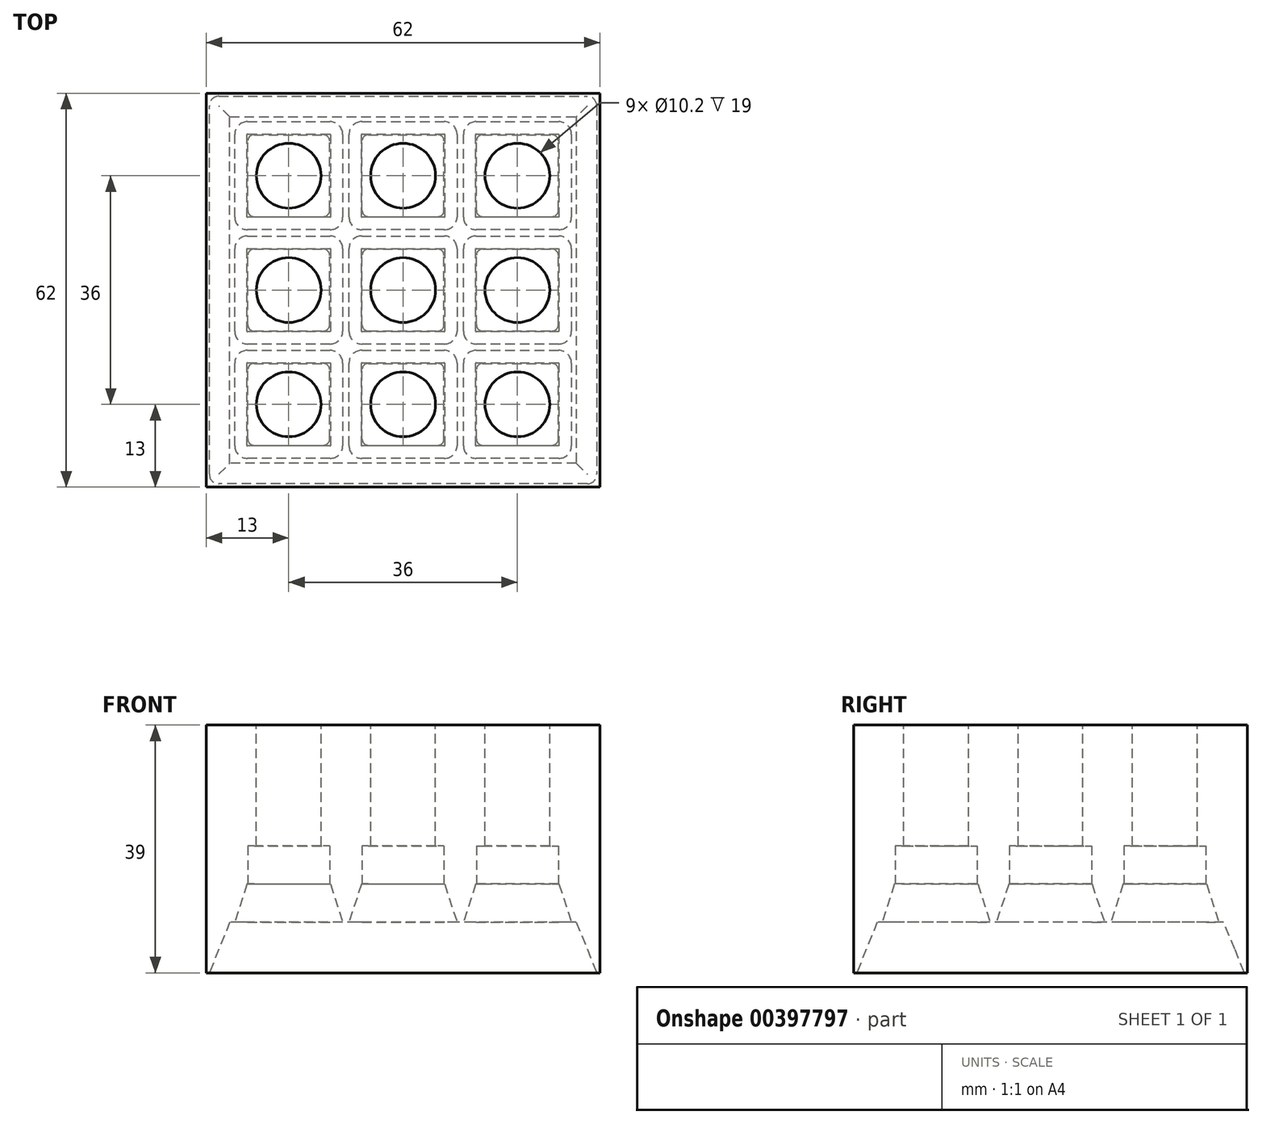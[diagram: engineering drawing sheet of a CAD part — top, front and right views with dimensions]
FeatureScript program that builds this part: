
annotation { "Feature Type Name" : "Feature", "Feature Type Description" : "" }
export const myFeature = defineFeature(function(context is Context, id is Id, definition is map)
    precondition{}
    {
        {
            var Q0;
            Q0=qCreatedBy(makeId("Top.planeOp"),FACE);
            var sketch = newSketch(context, id + "F0", { "sketchPlane" : qUnion([Q0])});
            skLineSegment(sketch, "E0.bottom", {"start": v(-31, 31) * mm, "end": v(31, 31) * mm});
            skLineSegment(sketch, "E0.top", {"start": v(-31, -31) * mm, "end": v(31, -31) * mm});
            skLineSegment(sketch, "E0.left", {"start": v(-31, 31) * mm, "end": v(-31, -31) * mm});
            skLineSegment(sketch, "E0.right", {"start": v(31, 31) * mm, "end": v(31, -31) * mm});
            skPoint(sketch, "E0.middle", {"position": v(0, 0) * mm});
            skSolve(sketch);
        }
        {
            var Q0;
            Q0=makeQuery(id+"F0.imprint","IMPRINT",FACE,{"disambiguationData":[TD([[makeQuery(id+"F0.imprint","IMPRINT",EDGE,{"derivedFrom":sQuery(id+"F0.wireOp",EDGE,"E0.bottom")}),-1.0]])]});
            extrude(context, id + "F1", {"entities" : qUnion([Q0]), "depth" : 39 * mm});
        }
        {
            var Q0;
            Q0=qCreatedBy(makeId("Top.planeOp"),FACE);
            cPlane(context, id + "F2", {"entities" : qUnion([Q0]), "cplaneType" : CPlaneType.OFFSET, "offset" : 8 * mm, "width" : 150 * mm, "height" : 150 * mm});
        }
        {
            var Q0;
            Q0=qCreatedBy(makeId("Top.planeOp"),FACE);
            var sketch = newSketch(context, id + "F3", { "sketchPlane" : qUnion([Q0])});
            skLineSegment(sketch, "E1.bottom", {"start": v(29, 30.5) * mm, "end": v(-29, 30.5) * mm});
            skLineSegment(sketch, "E1.top", {"start": v(29, -30.5) * mm, "end": v(-29, -30.5) * mm});
            skLineSegment(sketch, "E1.left", {"start": v(30.5, 29) * mm, "end": v(30.5, -29) * mm});
            skLineSegment(sketch, "E1.right", {"start": v(-30.5, 29) * mm, "end": v(-30.5, -29) * mm});
            skPoint(sketch, "E1.middle", {"position": v(0, 0) * mm});
            skPoint(sketch, "E2.visualSharp", {"position": v(30.5, -30.5) * mm});
            skArc(sketch, "E2.filletArc", {"start": v(29, -30.5) * mm, "mid": v(30.06, -30.06) * mm, "end": v(30.5, -29) * mm});
            skPoint(sketch, "E3.visualSharp", {"position": v(30.5, 30.5) * mm});
            skArc(sketch, "E3.filletArc", {"start": v(30.5, 29) * mm, "mid": v(30.06, 30.06) * mm, "end": v(29, 30.5) * mm});
            skPoint(sketch, "E4.visualSharp", {"position": v(-30.5, 30.5) * mm});
            skArc(sketch, "E4.filletArc", {"start": v(-29, 30.5) * mm, "mid": v(-30.06, 30.06) * mm, "end": v(-30.5, 29) * mm});
            skPoint(sketch, "E5.visualSharp", {"position": v(-30.5, -30.5) * mm});
            skArc(sketch, "E5.filletArc", {"start": v(-30.5, -29) * mm, "mid": v(-30.06, -30.06) * mm, "end": v(-29, -30.5) * mm});
            skSolve(sketch);
        }
        {
            var Q0;
            Q0 = qSketchRegion(id + "F3", true);
            extrude(context, id + "F4", {"entities" : qUnion([Q0]), "operationType" : NewBodyOperationType.REMOVE, "depth" : 8 * mm, "hasDraft" : true, "draftAngle" : 22 * degree, "draftPullDirection" : true});
        }
        {
            var Q0;
            Q0=qCreatedBy(id+"F2.planeOp",FACE);
            var sketch = newSketch(context, id + "F5", { "sketchPlane" : qUnion([Q0])});
            skLineSegment(sketch, "E6", {"start": v(0, -40.1) * mm, "end": v(0, 43.6) * mm, "construction": true});
            skLineSegment(sketch, "E7", {"start": v(42.56, 0) * mm, "end": v(-45.4, 0) * mm, "construction": true});
            skLineSegment(sketch, "E8", {"start": v(-18, -41.12) * mm, "end": v(-18, 43.04) * mm, "construction": true});
            skLineSegment(sketch, "E9", {"start": v(18, -41.98) * mm, "end": v(18, 43.76) * mm, "construction": true});
            skLineSegment(sketch, "E10", {"start": v(-42.81, -18) * mm, "end": v(38.4, -18) * mm, "construction": true});
            skLineSegment(sketch, "E11", {"start": v(-40.82, 18) * mm, "end": v(38.75, 18) * mm, "construction": true});
            skLineSegment(sketch, "E12.bottom", {"start": v(11.5, -9.5) * mm, "end": v(24.5, -9.5) * mm});
            skLineSegment(sketch, "E12.top", {"start": v(11.5, -26.5) * mm, "end": v(24.5, -26.5) * mm});
            skLineSegment(sketch, "E12.left", {"start": v(9.5, -11.5) * mm, "end": v(9.5, -24.5) * mm});
            skLineSegment(sketch, "E12.right", {"start": v(26.5, -11.5) * mm, "end": v(26.5, -24.5) * mm});
            skPoint(sketch, "E12.middle", {"position": v(18, -18) * mm});
            skPoint(sketch, "E13.visualSharp", {"position": v(26.5, -26.5) * mm});
            skArc(sketch, "E13.filletArc", {"start": v(24.5, -26.5) * mm, "mid": v(25.91, -25.91) * mm, "end": v(26.5, -24.5) * mm});
            skPoint(sketch, "E14.visualSharp", {"position": v(26.5, -9.5) * mm});
            skArc(sketch, "E14.filletArc", {"start": v(26.5, -11.5) * mm, "mid": v(25.91, -10.09) * mm, "end": v(24.5, -9.5) * mm});
            skPoint(sketch, "E15.visualSharp", {"position": v(9.5, -9.5) * mm});
            skArc(sketch, "E15.filletArc", {"start": v(11.5, -9.5) * mm, "mid": v(10.09, -10.09) * mm, "end": v(9.5, -11.5) * mm});
            skPoint(sketch, "E16.visualSharp", {"position": v(9.5, -26.5) * mm});
            skArc(sketch, "E16.filletArc", {"start": v(9.5, -24.5) * mm, "mid": v(10.09, -25.91) * mm, "end": v(11.5, -26.5) * mm});
            skPoint(sketch, "E17.0.1.0", {"position": v(9.5, 8.5) * mm});
            skPoint(sketch, "E17.0.1.1", {"position": v(9.5, -8.5) * mm});
            skPoint(sketch, "E17.0.1.2", {"position": v(26.5, -8.5) * mm});
            skPoint(sketch, "E17.0.1.3", {"position": v(26.5, 8.5) * mm});
            skPoint(sketch, "E17.0.1.4", {"position": v(18, 0) * mm});
            skLineSegment(sketch, "E17.0.1.5", {"start": v(26.5, 6.5) * mm, "end": v(26.5, -6.5) * mm});
            skLineSegment(sketch, "E17.0.1.6", {"start": v(9.5, 6.5) * mm, "end": v(9.5, -6.5) * mm});
            skLineSegment(sketch, "E17.0.1.7", {"start": v(11.5, 8.5) * mm, "end": v(24.5, 8.5) * mm});
            skLineSegment(sketch, "E17.0.1.8", {"start": v(11.5, -8.5) * mm, "end": v(24.5, -8.5) * mm});
            skArc(sketch, "E17.0.1.9", {"start": v(26.5, 6.5) * mm, "mid": v(25.91, 7.91) * mm, "end": v(24.5, 8.5) * mm});
            skArc(sketch, "E17.0.1.10", {"start": v(24.5, -8.5) * mm, "mid": v(25.91, -7.91) * mm, "end": v(26.5, -6.5) * mm});
            skArc(sketch, "E17.0.1.11", {"start": v(11.5, 8.5) * mm, "mid": v(10.09, 7.91) * mm, "end": v(9.5, 6.5) * mm});
            skArc(sketch, "E17.0.1.12", {"start": v(9.5, -6.5) * mm, "mid": v(10.09, -7.91) * mm, "end": v(11.5, -8.5) * mm});
            skPoint(sketch, "E17.0.2.0", {"position": v(9.5, 26.5) * mm});
            skPoint(sketch, "E17.0.2.1", {"position": v(9.5, 9.5) * mm});
            skPoint(sketch, "E17.0.2.2", {"position": v(26.5, 9.5) * mm});
            skPoint(sketch, "E17.0.2.3", {"position": v(26.5, 26.5) * mm});
            skPoint(sketch, "E17.0.2.4", {"position": v(18, 18) * mm});
            skLineSegment(sketch, "E17.0.2.5", {"start": v(26.5, 24.5) * mm, "end": v(26.5, 11.5) * mm});
            skLineSegment(sketch, "E17.0.2.6", {"start": v(9.5, 24.5) * mm, "end": v(9.5, 11.5) * mm});
            skLineSegment(sketch, "E17.0.2.7", {"start": v(11.5, 26.5) * mm, "end": v(24.5, 26.5) * mm});
            skLineSegment(sketch, "E17.0.2.8", {"start": v(11.5, 9.5) * mm, "end": v(24.5, 9.5) * mm});
            skArc(sketch, "E17.0.2.9", {"start": v(26.5, 24.5) * mm, "mid": v(25.91, 25.91) * mm, "end": v(24.5, 26.5) * mm});
            skArc(sketch, "E17.0.2.10", {"start": v(24.5, 9.5) * mm, "mid": v(25.91, 10.09) * mm, "end": v(26.5, 11.5) * mm});
            skArc(sketch, "E17.0.2.11", {"start": v(11.5, 26.5) * mm, "mid": v(10.09, 25.91) * mm, "end": v(9.5, 24.5) * mm});
            skArc(sketch, "E17.0.2.12", {"start": v(9.5, 11.5) * mm, "mid": v(10.09, 10.09) * mm, "end": v(11.5, 9.5) * mm});
            skPoint(sketch, "E17.1.0.0", {"position": v(-8.5, -9.5) * mm});
            skPoint(sketch, "E17.1.0.1", {"position": v(-8.5, -26.5) * mm});
            skPoint(sketch, "E17.1.0.2", {"position": v(8.5, -26.5) * mm});
            skPoint(sketch, "E17.1.0.3", {"position": v(8.5, -9.5) * mm});
            skPoint(sketch, "E17.1.0.4", {"position": v(0, -18) * mm});
            skLineSegment(sketch, "E17.1.0.5", {"start": v(8.5, -11.5) * mm, "end": v(8.5, -24.5) * mm});
            skLineSegment(sketch, "E17.1.0.6", {"start": v(-8.5, -11.5) * mm, "end": v(-8.5, -24.5) * mm});
            skLineSegment(sketch, "E17.1.0.7", {"start": v(-6.5, -9.5) * mm, "end": v(6.5, -9.5) * mm});
            skLineSegment(sketch, "E17.1.0.8", {"start": v(-6.5, -26.5) * mm, "end": v(6.5, -26.5) * mm});
            skArc(sketch, "E17.1.0.9", {"start": v(8.5, -11.5) * mm, "mid": v(7.91, -10.09) * mm, "end": v(6.5, -9.5) * mm});
            skArc(sketch, "E17.1.0.10", {"start": v(6.5, -26.5) * mm, "mid": v(7.91, -25.91) * mm, "end": v(8.5, -24.5) * mm});
            skArc(sketch, "E17.1.0.11", {"start": v(-6.5, -9.5) * mm, "mid": v(-7.91, -10.09) * mm, "end": v(-8.5, -11.5) * mm});
            skArc(sketch, "E17.1.0.12", {"start": v(-8.5, -24.5) * mm, "mid": v(-7.91, -25.91) * mm, "end": v(-6.5, -26.5) * mm});
            skPoint(sketch, "E17.1.1.0", {"position": v(-8.5, 8.5) * mm});
            skPoint(sketch, "E17.1.1.1", {"position": v(-8.5, -8.5) * mm});
            skPoint(sketch, "E17.1.1.2", {"position": v(8.5, -8.5) * mm});
            skPoint(sketch, "E17.1.1.3", {"position": v(8.5, 8.5) * mm});
            skPoint(sketch, "E17.1.1.4", {"position": v(0, 0) * mm});
            skLineSegment(sketch, "E17.1.1.5", {"start": v(8.5, 6.5) * mm, "end": v(8.5, -6.5) * mm});
            skLineSegment(sketch, "E17.1.1.6", {"start": v(-8.5, 6.5) * mm, "end": v(-8.5, -6.5) * mm});
            skLineSegment(sketch, "E17.1.1.7", {"start": v(-6.5, 8.5) * mm, "end": v(6.5, 8.5) * mm});
            skLineSegment(sketch, "E17.1.1.8", {"start": v(-6.5, -8.5) * mm, "end": v(6.5, -8.5) * mm});
            skArc(sketch, "E17.1.1.9", {"start": v(8.5, 6.5) * mm, "mid": v(7.91, 7.91) * mm, "end": v(6.5, 8.5) * mm});
            skArc(sketch, "E17.1.1.10", {"start": v(6.5, -8.5) * mm, "mid": v(7.91, -7.91) * mm, "end": v(8.5, -6.5) * mm});
            skArc(sketch, "E17.1.1.11", {"start": v(-6.5, 8.5) * mm, "mid": v(-7.91, 7.91) * mm, "end": v(-8.5, 6.5) * mm});
            skArc(sketch, "E17.1.1.12", {"start": v(-8.5, -6.5) * mm, "mid": v(-7.91, -7.91) * mm, "end": v(-6.5, -8.5) * mm});
            skPoint(sketch, "E17.1.2.0", {"position": v(-8.5, 26.5) * mm});
            skPoint(sketch, "E17.1.2.1", {"position": v(-8.5, 9.5) * mm});
            skPoint(sketch, "E17.1.2.2", {"position": v(8.5, 9.5) * mm});
            skPoint(sketch, "E17.1.2.3", {"position": v(8.5, 26.5) * mm});
            skPoint(sketch, "E17.1.2.4", {"position": v(0, 18) * mm});
            skLineSegment(sketch, "E17.1.2.5", {"start": v(8.5, 24.5) * mm, "end": v(8.5, 11.5) * mm});
            skLineSegment(sketch, "E17.1.2.6", {"start": v(-8.5, 24.5) * mm, "end": v(-8.5, 11.5) * mm});
            skLineSegment(sketch, "E17.1.2.7", {"start": v(-6.5, 26.5) * mm, "end": v(6.5, 26.5) * mm});
            skLineSegment(sketch, "E17.1.2.8", {"start": v(-6.5, 9.5) * mm, "end": v(6.5, 9.5) * mm});
            skArc(sketch, "E17.1.2.9", {"start": v(8.5, 24.5) * mm, "mid": v(7.91, 25.91) * mm, "end": v(6.5, 26.5) * mm});
            skArc(sketch, "E17.1.2.10", {"start": v(6.5, 9.5) * mm, "mid": v(7.91, 10.09) * mm, "end": v(8.5, 11.5) * mm});
            skArc(sketch, "E17.1.2.11", {"start": v(-6.5, 26.5) * mm, "mid": v(-7.91, 25.91) * mm, "end": v(-8.5, 24.5) * mm});
            skArc(sketch, "E17.1.2.12", {"start": v(-8.5, 11.5) * mm, "mid": v(-7.91, 10.09) * mm, "end": v(-6.5, 9.5) * mm});
            skPoint(sketch, "E17.2.0.0", {"position": v(-26.5, -9.5) * mm});
            skPoint(sketch, "E17.2.0.1", {"position": v(-26.5, -26.5) * mm});
            skPoint(sketch, "E17.2.0.2", {"position": v(-9.5, -26.5) * mm});
            skPoint(sketch, "E17.2.0.3", {"position": v(-9.5, -9.5) * mm});
            skPoint(sketch, "E17.2.0.4", {"position": v(-18, -18) * mm});
            skLineSegment(sketch, "E17.2.0.5", {"start": v(-9.5, -11.5) * mm, "end": v(-9.5, -24.5) * mm});
            skLineSegment(sketch, "E17.2.0.6", {"start": v(-26.5, -11.5) * mm, "end": v(-26.5, -24.5) * mm});
            skLineSegment(sketch, "E17.2.0.7", {"start": v(-24.5, -9.5) * mm, "end": v(-11.5, -9.5) * mm});
            skLineSegment(sketch, "E17.2.0.8", {"start": v(-24.5, -26.5) * mm, "end": v(-11.5, -26.5) * mm});
            skArc(sketch, "E17.2.0.9", {"start": v(-9.5, -11.5) * mm, "mid": v(-10.09, -10.09) * mm, "end": v(-11.5, -9.5) * mm});
            skArc(sketch, "E17.2.0.10", {"start": v(-11.5, -26.5) * mm, "mid": v(-10.09, -25.91) * mm, "end": v(-9.5, -24.5) * mm});
            skArc(sketch, "E17.2.0.11", {"start": v(-24.5, -9.5) * mm, "mid": v(-25.91, -10.09) * mm, "end": v(-26.5, -11.5) * mm});
            skArc(sketch, "E17.2.0.12", {"start": v(-26.5, -24.5) * mm, "mid": v(-25.91, -25.91) * mm, "end": v(-24.5, -26.5) * mm});
            skPoint(sketch, "E17.2.1.0", {"position": v(-26.5, 8.5) * mm});
            skPoint(sketch, "E17.2.1.1", {"position": v(-26.5, -8.5) * mm});
            skPoint(sketch, "E17.2.1.2", {"position": v(-9.5, -8.5) * mm});
            skPoint(sketch, "E17.2.1.3", {"position": v(-9.5, 8.5) * mm});
            skPoint(sketch, "E17.2.1.4", {"position": v(-18, 0) * mm});
            skLineSegment(sketch, "E17.2.1.5", {"start": v(-9.5, 6.5) * mm, "end": v(-9.5, -6.5) * mm});
            skLineSegment(sketch, "E17.2.1.6", {"start": v(-26.5, 6.5) * mm, "end": v(-26.5, -6.5) * mm});
            skLineSegment(sketch, "E17.2.1.7", {"start": v(-24.5, 8.5) * mm, "end": v(-11.5, 8.5) * mm});
            skLineSegment(sketch, "E17.2.1.8", {"start": v(-24.5, -8.5) * mm, "end": v(-11.5, -8.5) * mm});
            skArc(sketch, "E17.2.1.9", {"start": v(-9.5, 6.5) * mm, "mid": v(-10.09, 7.91) * mm, "end": v(-11.5, 8.5) * mm});
            skArc(sketch, "E17.2.1.10", {"start": v(-11.5, -8.5) * mm, "mid": v(-10.09, -7.91) * mm, "end": v(-9.5, -6.5) * mm});
            skArc(sketch, "E17.2.1.11", {"start": v(-24.5, 8.5) * mm, "mid": v(-25.91, 7.91) * mm, "end": v(-26.5, 6.5) * mm});
            skArc(sketch, "E17.2.1.12", {"start": v(-26.5, -6.5) * mm, "mid": v(-25.91, -7.91) * mm, "end": v(-24.5, -8.5) * mm});
            skPoint(sketch, "E17.2.2.0", {"position": v(-26.5, 26.5) * mm});
            skPoint(sketch, "E17.2.2.1", {"position": v(-26.5, 9.5) * mm});
            skPoint(sketch, "E17.2.2.2", {"position": v(-9.5, 9.5) * mm});
            skPoint(sketch, "E17.2.2.3", {"position": v(-9.5, 26.5) * mm});
            skPoint(sketch, "E17.2.2.4", {"position": v(-18, 18) * mm});
            skLineSegment(sketch, "E17.2.2.5", {"start": v(-9.5, 24.5) * mm, "end": v(-9.5, 11.5) * mm});
            skLineSegment(sketch, "E17.2.2.6", {"start": v(-26.5, 24.5) * mm, "end": v(-26.5, 11.5) * mm});
            skLineSegment(sketch, "E17.2.2.7", {"start": v(-24.5, 26.5) * mm, "end": v(-11.5, 26.5) * mm});
            skLineSegment(sketch, "E17.2.2.8", {"start": v(-24.5, 9.5) * mm, "end": v(-11.5, 9.5) * mm});
            skArc(sketch, "E17.2.2.9", {"start": v(-9.5, 24.5) * mm, "mid": v(-10.09, 25.91) * mm, "end": v(-11.5, 26.5) * mm});
            skArc(sketch, "E17.2.2.10", {"start": v(-11.5, 9.5) * mm, "mid": v(-10.09, 10.09) * mm, "end": v(-9.5, 11.5) * mm});
            skArc(sketch, "E17.2.2.11", {"start": v(-24.5, 26.5) * mm, "mid": v(-25.91, 25.91) * mm, "end": v(-26.5, 24.5) * mm});
            skArc(sketch, "E17.2.2.12", {"start": v(-26.5, 11.5) * mm, "mid": v(-25.91, 10.09) * mm, "end": v(-24.5, 9.5) * mm});
            skLineSegment(sketch, "E17.direction1", {"start": v(9.5, -26.5) * mm, "end": v(-8.5, -26.5) * mm, "construction": true});
            skLineSegment(sketch, "E17.direction2", {"start": v(9.5, -26.5) * mm, "end": v(9.5, -8.5) * mm, "construction": true});
            skSolve(sketch);
        }
        {
            var Q0;
            Q0=makeQuery(id+"F5.imprint","IMPRINT",FACE,{"disambiguationData":[TD([[makeQuery(id+"F5.imprint","IMPRINT",EDGE,{"derivedFrom":sQuery(id+"F5.wireOp",EDGE,"E17.2.0.5")}),-1.0]])]});
            var Q1;
            Q1=makeQuery(id+"F5.imprint","IMPRINT",FACE,{"disambiguationData":[TD([[makeQuery(id+"F5.imprint","IMPRINT",EDGE,{"derivedFrom":sQuery(id+"F5.wireOp",EDGE,"E17.1.0.5")}),-1.0]])]});
            var Q2;
            Q2=makeQuery(id+"F5.imprint","IMPRINT",FACE,{"disambiguationData":[TD([[makeQuery(id+"F5.imprint","IMPRINT",EDGE,{"derivedFrom":sQuery(id+"F5.wireOp",EDGE,"E12.bottom")}),-1.0]])]});
            var Q3;
            Q3=makeQuery(id+"F5.imprint","IMPRINT",FACE,{"disambiguationData":[TD([[makeQuery(id+"F5.imprint","IMPRINT",EDGE,{"derivedFrom":sQuery(id+"F5.wireOp",EDGE,"E17.0.1.5")}),-1.0]])]});
            var Q4;
            Q4=makeQuery(id+"F5.imprint","IMPRINT",FACE,{"disambiguationData":[TD([[makeQuery(id+"F5.imprint","IMPRINT",EDGE,{"derivedFrom":sQuery(id+"F5.wireOp",EDGE,"E17.1.1.5")}),-1.0]])]});
            var Q5;
            Q5=makeQuery(id+"F5.imprint","IMPRINT",FACE,{"disambiguationData":[TD([[makeQuery(id+"F5.imprint","IMPRINT",EDGE,{"derivedFrom":sQuery(id+"F5.wireOp",EDGE,"E17.2.1.5")}),-1.0]])]});
            var Q6;
            Q6=makeQuery(id+"F5.imprint","IMPRINT",FACE,{"disambiguationData":[TD([[makeQuery(id+"F5.imprint","IMPRINT",EDGE,{"derivedFrom":sQuery(id+"F5.wireOp",EDGE,"E17.2.2.5")}),-1.0]])]});
            var Q7;
            Q7=makeQuery(id+"F5.imprint","IMPRINT",FACE,{"disambiguationData":[TD([[makeQuery(id+"F5.imprint","IMPRINT",EDGE,{"derivedFrom":sQuery(id+"F5.wireOp",EDGE,"E17.1.2.5")}),-1.0]])]});
            var Q8;
            Q8=makeQuery(id+"F5.imprint","IMPRINT",FACE,{"disambiguationData":[TD([[makeQuery(id+"F5.imprint","IMPRINT",EDGE,{"derivedFrom":sQuery(id+"F5.wireOp",EDGE,"E17.0.2.5")}),-1.0]])]});
            extrude(context, id + "F6", {"entities" : qUnion([Q0, Q1, Q2, Q3, Q4, Q5, Q6, Q7, Q8]), "operationType" : NewBodyOperationType.REMOVE, "depth" : 6 * mm, "hasDraft" : true, "draftAngle" : 18 * degree, "draftPullDirection" : true});
        }
        {
            var Q0;
            Q0=qCreatedBy(id+"F2.planeOp",FACE);
            cPlane(context, id + "F7", {"entities" : qUnion([Q0]), "cplaneType" : CPlaneType.OFFSET, "offset" : 6 * mm, "width" : 150 * mm, "height" : 150 * mm});
        }
        {
            var Q0;
            Q0=qCreatedBy(id+"F7.planeOp",FACE);
            var sketch = newSketch(context, id + "F8", { "sketchPlane" : qUnion([Q0])});
            skLineSegment(sketch, "E18", {"start": v(34.11, 0) * mm, "end": v(-34.3, 0) * mm, "construction": true});
            skLineSegment(sketch, "E19", {"start": v(0, -32.93) * mm, "end": v(0, 33.45) * mm, "construction": true});
            skLineSegment(sketch, "E20", {"start": v(33.88, -18) * mm, "end": v(-33.04, -18) * mm, "construction": true});
            skLineSegment(sketch, "E21", {"start": v(18, -34.67) * mm, "end": v(18, 34.86) * mm, "construction": true});
            skLineSegment(sketch, "E22.direction1", {"start": v(18, -18) * mm, "end": v(0, -18) * mm, "construction": true});
            skLineSegment(sketch, "E22.direction2", {"start": v(18, -18) * mm, "end": v(18, 0) * mm, "construction": true});
            skLineSegment(sketch, "E23.bottom", {"start": v(12.55, -24.45) * mm, "end": v(23.45, -24.45) * mm});
            skLineSegment(sketch, "E23.top", {"start": v(12.55, -11.55) * mm, "end": v(23.45, -11.55) * mm});
            skLineSegment(sketch, "E23.left", {"start": v(11.55, -23.45) * mm, "end": v(11.55, -12.55) * mm});
            skLineSegment(sketch, "E23.right", {"start": v(24.45, -23.45) * mm, "end": v(24.45, -12.55) * mm});
            skPoint(sketch, "E23.middle", {"position": v(18, -18) * mm});
            skPoint(sketch, "E24.visualSharp", {"position": v(24.45, -24.45) * mm});
            skArc(sketch, "E24.filletArc", {"start": v(23.45, -24.45) * mm, "mid": v(24.16, -24.16) * mm, "end": v(24.45, -23.45) * mm});
            skPoint(sketch, "E25.visualSharp", {"position": v(11.55, -24.45) * mm});
            skArc(sketch, "E25.filletArc", {"start": v(11.55, -23.45) * mm, "mid": v(11.84, -24.16) * mm, "end": v(12.55, -24.45) * mm});
            skPoint(sketch, "E26.visualSharp", {"position": v(11.55, -11.55) * mm});
            skArc(sketch, "E26.filletArc", {"start": v(12.55, -11.55) * mm, "mid": v(11.84, -11.84) * mm, "end": v(11.55, -12.55) * mm});
            skPoint(sketch, "E27.visualSharp", {"position": v(24.45, -11.55) * mm});
            skArc(sketch, "E27.filletArc", {"start": v(24.45, -12.55) * mm, "mid": v(24.16, -11.84) * mm, "end": v(23.45, -11.55) * mm});
            skPoint(sketch, "E28.0.1.0", {"position": v(24.45, -6.45) * mm});
            skPoint(sketch, "E28.0.1.1", {"position": v(24.45, 6.45) * mm});
            skPoint(sketch, "E28.0.1.2", {"position": v(11.55, 6.45) * mm});
            skPoint(sketch, "E28.0.1.3", {"position": v(18, 0) * mm});
            skLineSegment(sketch, "E28.0.1.4", {"start": v(11.55, -5.45) * mm, "end": v(11.55, 5.45) * mm});
            skLineSegment(sketch, "E28.0.1.5", {"start": v(12.55, -6.45) * mm, "end": v(23.45, -6.45) * mm});
            skPoint(sketch, "E28.0.1.6", {"position": v(11.55, -6.45) * mm});
            skLineSegment(sketch, "E28.0.1.7", {"start": v(24.45, -5.45) * mm, "end": v(24.45, 5.45) * mm});
            skLineSegment(sketch, "E28.0.1.8", {"start": v(12.55, 6.45) * mm, "end": v(23.45, 6.45) * mm});
            skArc(sketch, "E28.0.1.9", {"start": v(24.45, 5.45) * mm, "mid": v(24.16, 6.16) * mm, "end": v(23.45, 6.45) * mm});
            skArc(sketch, "E28.0.1.10", {"start": v(12.55, 6.45) * mm, "mid": v(11.84, 6.16) * mm, "end": v(11.55, 5.45) * mm});
            skArc(sketch, "E28.0.1.11", {"start": v(23.45, -6.45) * mm, "mid": v(24.16, -6.16) * mm, "end": v(24.45, -5.45) * mm});
            skArc(sketch, "E28.0.1.12", {"start": v(11.55, -5.45) * mm, "mid": v(11.84, -6.16) * mm, "end": v(12.55, -6.45) * mm});
            skPoint(sketch, "E28.0.2.0", {"position": v(24.45, 11.55) * mm});
            skPoint(sketch, "E28.0.2.1", {"position": v(24.45, 24.45) * mm});
            skPoint(sketch, "E28.0.2.2", {"position": v(11.55, 24.45) * mm});
            skPoint(sketch, "E28.0.2.3", {"position": v(18, 18) * mm});
            skLineSegment(sketch, "E28.0.2.4", {"start": v(11.55, 12.55) * mm, "end": v(11.55, 23.45) * mm});
            skLineSegment(sketch, "E28.0.2.5", {"start": v(12.55, 11.55) * mm, "end": v(23.45, 11.55) * mm});
            skPoint(sketch, "E28.0.2.6", {"position": v(11.55, 11.55) * mm});
            skLineSegment(sketch, "E28.0.2.7", {"start": v(24.45, 12.55) * mm, "end": v(24.45, 23.45) * mm});
            skLineSegment(sketch, "E28.0.2.8", {"start": v(12.55, 24.45) * mm, "end": v(23.45, 24.45) * mm});
            skArc(sketch, "E28.0.2.9", {"start": v(24.45, 23.45) * mm, "mid": v(24.16, 24.16) * mm, "end": v(23.45, 24.45) * mm});
            skArc(sketch, "E28.0.2.10", {"start": v(12.55, 24.45) * mm, "mid": v(11.84, 24.16) * mm, "end": v(11.55, 23.45) * mm});
            skArc(sketch, "E28.0.2.11", {"start": v(23.45, 11.55) * mm, "mid": v(24.16, 11.84) * mm, "end": v(24.45, 12.55) * mm});
            skArc(sketch, "E28.0.2.12", {"start": v(11.55, 12.55) * mm, "mid": v(11.84, 11.84) * mm, "end": v(12.55, 11.55) * mm});
            skPoint(sketch, "E28.1.0.0", {"position": v(6.45, -24.45) * mm});
            skPoint(sketch, "E28.1.0.1", {"position": v(6.45, -11.55) * mm});
            skPoint(sketch, "E28.1.0.2", {"position": v(-6.45, -11.55) * mm});
            skPoint(sketch, "E28.1.0.3", {"position": v(0, -18) * mm});
            skLineSegment(sketch, "E28.1.0.4", {"start": v(-6.45, -23.45) * mm, "end": v(-6.45, -12.55) * mm});
            skLineSegment(sketch, "E28.1.0.5", {"start": v(-5.45, -24.45) * mm, "end": v(5.45, -24.45) * mm});
            skPoint(sketch, "E28.1.0.6", {"position": v(-6.45, -24.45) * mm});
            skLineSegment(sketch, "E28.1.0.7", {"start": v(6.45, -23.45) * mm, "end": v(6.45, -12.55) * mm});
            skLineSegment(sketch, "E28.1.0.8", {"start": v(-5.45, -11.55) * mm, "end": v(5.45, -11.55) * mm});
            skArc(sketch, "E28.1.0.9", {"start": v(6.45, -12.55) * mm, "mid": v(6.16, -11.84) * mm, "end": v(5.45, -11.55) * mm});
            skArc(sketch, "E28.1.0.10", {"start": v(-5.45, -11.55) * mm, "mid": v(-6.16, -11.84) * mm, "end": v(-6.45, -12.55) * mm});
            skArc(sketch, "E28.1.0.11", {"start": v(5.45, -24.45) * mm, "mid": v(6.16, -24.16) * mm, "end": v(6.45, -23.45) * mm});
            skArc(sketch, "E28.1.0.12", {"start": v(-6.45, -23.45) * mm, "mid": v(-6.16, -24.16) * mm, "end": v(-5.45, -24.45) * mm});
            skPoint(sketch, "E28.1.1.0", {"position": v(6.45, -6.45) * mm});
            skPoint(sketch, "E28.1.1.1", {"position": v(6.45, 6.45) * mm});
            skPoint(sketch, "E28.1.1.2", {"position": v(-6.45, 6.45) * mm});
            skPoint(sketch, "E28.1.1.3", {"position": v(0, 0) * mm});
            skLineSegment(sketch, "E28.1.1.4", {"start": v(-6.45, -5.45) * mm, "end": v(-6.45, 5.45) * mm});
            skLineSegment(sketch, "E28.1.1.5", {"start": v(-5.45, -6.45) * mm, "end": v(5.45, -6.45) * mm});
            skPoint(sketch, "E28.1.1.6", {"position": v(-6.45, -6.45) * mm});
            skLineSegment(sketch, "E28.1.1.7", {"start": v(6.45, -5.45) * mm, "end": v(6.45, 5.45) * mm});
            skLineSegment(sketch, "E28.1.1.8", {"start": v(-5.45, 6.45) * mm, "end": v(5.45, 6.45) * mm});
            skArc(sketch, "E28.1.1.9", {"start": v(6.45, 5.45) * mm, "mid": v(6.16, 6.16) * mm, "end": v(5.45, 6.45) * mm});
            skArc(sketch, "E28.1.1.10", {"start": v(-5.45, 6.45) * mm, "mid": v(-6.16, 6.16) * mm, "end": v(-6.45, 5.45) * mm});
            skArc(sketch, "E28.1.1.11", {"start": v(5.45, -6.45) * mm, "mid": v(6.16, -6.16) * mm, "end": v(6.45, -5.45) * mm});
            skArc(sketch, "E28.1.1.12", {"start": v(-6.45, -5.45) * mm, "mid": v(-6.16, -6.16) * mm, "end": v(-5.45, -6.45) * mm});
            skPoint(sketch, "E28.1.2.0", {"position": v(6.45, 11.55) * mm});
            skPoint(sketch, "E28.1.2.1", {"position": v(6.45, 24.45) * mm});
            skPoint(sketch, "E28.1.2.2", {"position": v(-6.45, 24.45) * mm});
            skPoint(sketch, "E28.1.2.3", {"position": v(0, 18) * mm});
            skLineSegment(sketch, "E28.1.2.4", {"start": v(-6.45, 12.55) * mm, "end": v(-6.45, 23.45) * mm});
            skLineSegment(sketch, "E28.1.2.5", {"start": v(-5.45, 11.55) * mm, "end": v(5.45, 11.55) * mm});
            skPoint(sketch, "E28.1.2.6", {"position": v(-6.45, 11.55) * mm});
            skLineSegment(sketch, "E28.1.2.7", {"start": v(6.45, 12.55) * mm, "end": v(6.45, 23.45) * mm});
            skLineSegment(sketch, "E28.1.2.8", {"start": v(-5.45, 24.45) * mm, "end": v(5.45, 24.45) * mm});
            skArc(sketch, "E28.1.2.9", {"start": v(6.45, 23.45) * mm, "mid": v(6.16, 24.16) * mm, "end": v(5.45, 24.45) * mm});
            skArc(sketch, "E28.1.2.10", {"start": v(-5.45, 24.45) * mm, "mid": v(-6.16, 24.16) * mm, "end": v(-6.45, 23.45) * mm});
            skArc(sketch, "E28.1.2.11", {"start": v(5.45, 11.55) * mm, "mid": v(6.16, 11.84) * mm, "end": v(6.45, 12.55) * mm});
            skArc(sketch, "E28.1.2.12", {"start": v(-6.45, 12.55) * mm, "mid": v(-6.16, 11.84) * mm, "end": v(-5.45, 11.55) * mm});
            skPoint(sketch, "E28.2.0.0", {"position": v(-11.55, -24.45) * mm});
            skPoint(sketch, "E28.2.0.1", {"position": v(-11.55, -11.55) * mm});
            skPoint(sketch, "E28.2.0.2", {"position": v(-24.45, -11.55) * mm});
            skPoint(sketch, "E28.2.0.3", {"position": v(-18, -18) * mm});
            skLineSegment(sketch, "E28.2.0.4", {"start": v(-24.45, -23.45) * mm, "end": v(-24.45, -12.55) * mm});
            skLineSegment(sketch, "E28.2.0.5", {"start": v(-23.45, -24.45) * mm, "end": v(-12.55, -24.45) * mm});
            skPoint(sketch, "E28.2.0.6", {"position": v(-24.45, -24.45) * mm});
            skLineSegment(sketch, "E28.2.0.7", {"start": v(-11.55, -23.45) * mm, "end": v(-11.55, -12.55) * mm});
            skLineSegment(sketch, "E28.2.0.8", {"start": v(-23.45, -11.55) * mm, "end": v(-12.55, -11.55) * mm});
            skArc(sketch, "E28.2.0.9", {"start": v(-11.55, -12.55) * mm, "mid": v(-11.84, -11.84) * mm, "end": v(-12.55, -11.55) * mm});
            skArc(sketch, "E28.2.0.10", {"start": v(-23.45, -11.55) * mm, "mid": v(-24.16, -11.84) * mm, "end": v(-24.45, -12.55) * mm});
            skArc(sketch, "E28.2.0.11", {"start": v(-12.55, -24.45) * mm, "mid": v(-11.84, -24.16) * mm, "end": v(-11.55, -23.45) * mm});
            skArc(sketch, "E28.2.0.12", {"start": v(-24.45, -23.45) * mm, "mid": v(-24.16, -24.16) * mm, "end": v(-23.45, -24.45) * mm});
            skPoint(sketch, "E28.2.1.0", {"position": v(-11.55, -6.45) * mm});
            skPoint(sketch, "E28.2.1.1", {"position": v(-11.55, 6.45) * mm});
            skPoint(sketch, "E28.2.1.2", {"position": v(-24.45, 6.45) * mm});
            skPoint(sketch, "E28.2.1.3", {"position": v(-18, 0) * mm});
            skLineSegment(sketch, "E28.2.1.4", {"start": v(-24.45, -5.45) * mm, "end": v(-24.45, 5.45) * mm});
            skLineSegment(sketch, "E28.2.1.5", {"start": v(-23.45, -6.45) * mm, "end": v(-12.55, -6.45) * mm});
            skPoint(sketch, "E28.2.1.6", {"position": v(-24.45, -6.45) * mm});
            skLineSegment(sketch, "E28.2.1.7", {"start": v(-11.55, -5.45) * mm, "end": v(-11.55, 5.45) * mm});
            skLineSegment(sketch, "E28.2.1.8", {"start": v(-23.45, 6.45) * mm, "end": v(-12.55, 6.45) * mm});
            skArc(sketch, "E28.2.1.9", {"start": v(-11.55, 5.45) * mm, "mid": v(-11.84, 6.16) * mm, "end": v(-12.55, 6.45) * mm});
            skArc(sketch, "E28.2.1.10", {"start": v(-23.45, 6.45) * mm, "mid": v(-24.16, 6.16) * mm, "end": v(-24.45, 5.45) * mm});
            skArc(sketch, "E28.2.1.11", {"start": v(-12.55, -6.45) * mm, "mid": v(-11.84, -6.16) * mm, "end": v(-11.55, -5.45) * mm});
            skArc(sketch, "E28.2.1.12", {"start": v(-24.45, -5.45) * mm, "mid": v(-24.16, -6.16) * mm, "end": v(-23.45, -6.45) * mm});
            skPoint(sketch, "E28.2.2.0", {"position": v(-11.55, 11.55) * mm});
            skPoint(sketch, "E28.2.2.1", {"position": v(-11.55, 24.45) * mm});
            skPoint(sketch, "E28.2.2.2", {"position": v(-24.45, 24.45) * mm});
            skPoint(sketch, "E28.2.2.3", {"position": v(-18, 18) * mm});
            skLineSegment(sketch, "E28.2.2.4", {"start": v(-24.45, 12.55) * mm, "end": v(-24.45, 23.45) * mm});
            skLineSegment(sketch, "E28.2.2.5", {"start": v(-23.45, 11.55) * mm, "end": v(-12.55, 11.55) * mm});
            skPoint(sketch, "E28.2.2.6", {"position": v(-24.45, 11.55) * mm});
            skLineSegment(sketch, "E28.2.2.7", {"start": v(-11.55, 12.55) * mm, "end": v(-11.55, 23.45) * mm});
            skLineSegment(sketch, "E28.2.2.8", {"start": v(-23.45, 24.45) * mm, "end": v(-12.55, 24.45) * mm});
            skArc(sketch, "E28.2.2.9", {"start": v(-11.55, 23.45) * mm, "mid": v(-11.84, 24.16) * mm, "end": v(-12.55, 24.45) * mm});
            skArc(sketch, "E28.2.2.10", {"start": v(-23.45, 24.45) * mm, "mid": v(-24.16, 24.16) * mm, "end": v(-24.45, 23.45) * mm});
            skArc(sketch, "E28.2.2.11", {"start": v(-12.55, 11.55) * mm, "mid": v(-11.84, 11.84) * mm, "end": v(-11.55, 12.55) * mm});
            skArc(sketch, "E28.2.2.12", {"start": v(-24.45, 12.55) * mm, "mid": v(-24.16, 11.84) * mm, "end": v(-23.45, 11.55) * mm});
            skLineSegment(sketch, "E28.direction1", {"start": v(11.55, -24.45) * mm, "end": v(-6.45, -24.45) * mm, "construction": true});
            skLineSegment(sketch, "E28.direction2", {"start": v(11.55, -24.45) * mm, "end": v(11.55, -6.45) * mm, "construction": true});
            skSolve(sketch);
        }
        {
            var Q0;
            Q0 = qSketchRegion(id + "F8", true);
            extrude(context, id + "F9", {"entities" : qUnion([Q0]), "operationType" : NewBodyOperationType.REMOVE, "depth" : 6 * mm});
        }
        {
            var Q0;
            Q0=qCreatedBy(id+"F7.planeOp",FACE);
            cPlane(context, id + "F10", {"entities" : qUnion([Q0]), "cplaneType" : CPlaneType.OFFSET, "offset" : 25 * mm, "width" : 150 * mm, "height" : 150 * mm});
        }
        {
            var Q0;
            Q0=qCreatedBy(id+"F10.planeOp",FACE);
            var sketch = newSketch(context, id + "F11", { "sketchPlane" : qUnion([Q0])});
            skLineSegment(sketch, "E29", {"start": v(0, 35.42) * mm, "end": v(0, -39.05) * mm, "construction": true});
            skLineSegment(sketch, "E30", {"start": v(18, 38.47) * mm, "end": v(18, -39.22) * mm, "construction": true});
            skLineSegment(sketch, "E31", {"start": v(-37.81, 0) * mm, "end": v(41.24, 0) * mm, "construction": true});
            skLineSegment(sketch, "E32", {"start": v(-37.64, 18) * mm, "end": v(41.07, 18) * mm, "construction": true});
            skCircle(sketch, "E33", {"center": v(18, 18) * mm, "radius": 5.1 * mm});
            skCircle(sketch, "E34.0.1.0", {"center": v(18, 0) * mm, "radius": 5.1 * mm});
            skCircle(sketch, "E34.0.2.0", {"center": v(18, -18) * mm, "radius": 5.1 * mm});
            skCircle(sketch, "E34.1.0.0", {"center": v(0, 18) * mm, "radius": 5.1 * mm});
            skCircle(sketch, "E34.1.1.0", {"center": v(0, 0) * mm, "radius": 5.1 * mm});
            skCircle(sketch, "E34.1.2.0", {"center": v(0, -18) * mm, "radius": 5.1 * mm});
            skCircle(sketch, "E34.2.0.0", {"center": v(-18, 18) * mm, "radius": 5.1 * mm});
            skCircle(sketch, "E34.2.1.0", {"center": v(-18, 0) * mm, "radius": 5.1 * mm});
            skCircle(sketch, "E34.2.2.0", {"center": v(-18, -18) * mm, "radius": 5.1 * mm});
            skLineSegment(sketch, "E34.direction1", {"start": v(18, 18) * mm, "end": v(0, 18) * mm, "construction": true});
            skLineSegment(sketch, "E34.direction2", {"start": v(18, 18) * mm, "end": v(18, 0) * mm, "construction": true});
            skSolve(sketch);
        }
        {
            var Q0;
            Q0=makeQuery(id+"F11.imprint","IMPRINT",FACE,{"disambiguationData":[TD([[makeQuery(id+"F11.imprint","IMPRINT",EDGE,{"derivedFrom":sQuery(id+"F11.wireOp",EDGE,"E33")}),1.0]])]});
            var Q1;
            Q1=makeQuery(id+"F11.imprint","IMPRINT",FACE,{"disambiguationData":[TD([[makeQuery(id+"F11.imprint","IMPRINT",EDGE,{"derivedFrom":sQuery(id+"F11.wireOp",EDGE,"E34.1.0.0")}),1.0]])]});
            var Q2;
            Q2=makeQuery(id+"F11.imprint","IMPRINT",FACE,{"disambiguationData":[TD([[makeQuery(id+"F11.imprint","IMPRINT",EDGE,{"derivedFrom":sQuery(id+"F11.wireOp",EDGE,"E34.2.0.0")}),1.0]])]});
            var Q3;
            Q3=makeQuery(id+"F11.imprint","IMPRINT",FACE,{"disambiguationData":[TD([[makeQuery(id+"F11.imprint","IMPRINT",EDGE,{"derivedFrom":sQuery(id+"F11.wireOp",EDGE,"E34.2.1.0")}),1.0]])]});
            var Q4;
            Q4=makeQuery(id+"F11.imprint","IMPRINT",FACE,{"disambiguationData":[TD([[makeQuery(id+"F11.imprint","IMPRINT",EDGE,{"derivedFrom":sQuery(id+"F11.wireOp",EDGE,"E34.1.1.0")}),1.0]])]});
            var Q5;
            Q5=makeQuery(id+"F11.imprint","IMPRINT",FACE,{"disambiguationData":[TD([[makeQuery(id+"F11.imprint","IMPRINT",EDGE,{"derivedFrom":sQuery(id+"F11.wireOp",EDGE,"E34.0.1.0")}),1.0]])]});
            var Q6;
            Q6=makeQuery(id+"F11.imprint","IMPRINT",FACE,{"disambiguationData":[TD([[makeQuery(id+"F11.imprint","IMPRINT",EDGE,{"derivedFrom":sQuery(id+"F11.wireOp",EDGE,"E34.0.2.0")}),1.0]])]});
            var Q7;
            Q7=makeQuery(id+"F11.imprint","IMPRINT",FACE,{"disambiguationData":[TD([[makeQuery(id+"F11.imprint","IMPRINT",EDGE,{"derivedFrom":sQuery(id+"F11.wireOp",EDGE,"E34.1.2.0")}),1.0]])]});
            var Q8;
            Q8=makeQuery(id+"F11.imprint","IMPRINT",FACE,{"disambiguationData":[TD([[makeQuery(id+"F11.imprint","IMPRINT",EDGE,{"derivedFrom":sQuery(id+"F11.wireOp",EDGE,"E34.2.2.0")}),1.0]])]});
            var Q9;
            Q9=sQuery(id+"F11.wireOp",EDGE,"E33");
            extrude(context, id + "F12", {"entities" : qUnion([Q0, Q1, Q2, Q3, Q4, Q5, Q6, Q7, Q8]), "operationType" : NewBodyOperationType.REMOVE, "surfaceEntities" : qUnion([Q9]), "oppositeDirection" : true, "depth" : 19 * mm});
        }
    });
